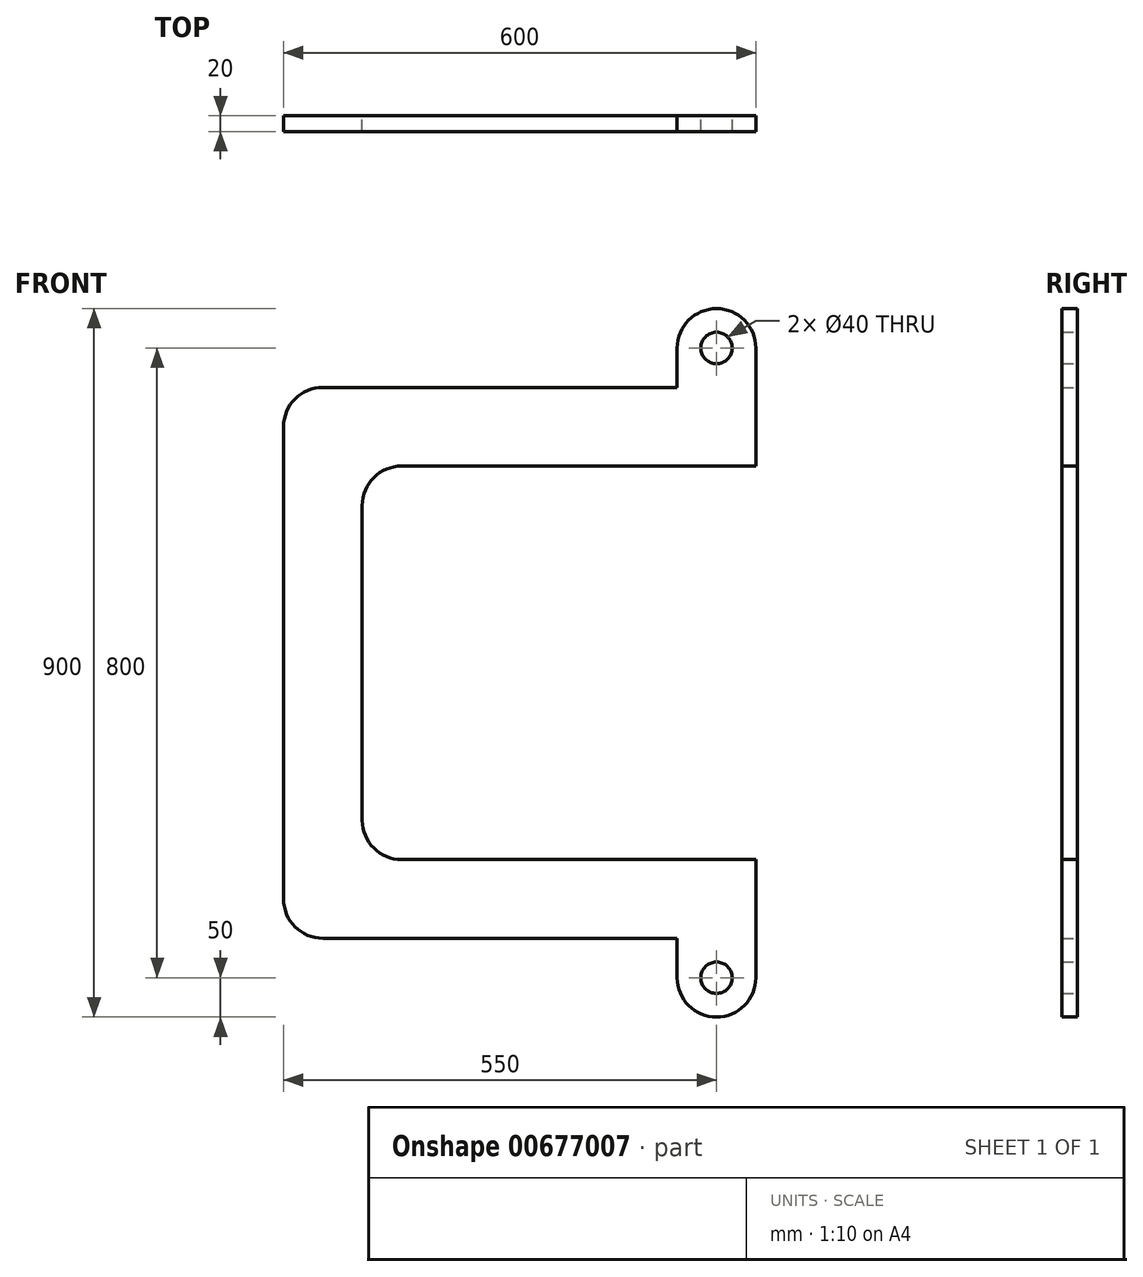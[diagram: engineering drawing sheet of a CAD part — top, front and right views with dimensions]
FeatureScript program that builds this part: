
annotation { "Feature Type Name" : "Feature", "Feature Type Description" : "" }
export const myFeature = defineFeature(function(context is Context, id is Id, definition is map)
    precondition{}
    {
        {
            var Q0;
            Q0=qCreatedBy(makeId("Front.planeOp"),FACE);
            var sketch = newSketch(context, id + "F0", { "sketchPlane" : qUnion([Q0])});
            skLineSegment(sketch, "E0", {"start": v(0, 0) * mm, "end": v(0, 300) * mm});
            skLineSegment(sketch, "E1", {"start": v(50, 350) * mm, "end": v(500, 350) * mm});
            skLineSegment(sketch, "E2", {"start": v(500, 350) * mm, "end": v(500, 400) * mm});
            skLineSegment(sketch, "E3", {"start": v(600, 400) * mm, "end": v(600, 250) * mm});
            skLineSegment(sketch, "E4", {"start": v(600, 250) * mm, "end": v(150, 250) * mm});
            skLineSegment(sketch, "E5", {"start": v(100, 200) * mm, "end": v(100, 0) * mm});
            skArc(sketch, "E6", {"start": v(600, 400) * mm, "mid": v(550, 450) * mm, "end": v(500, 400) * mm});
            skPoint(sketch, "E6.third.point", {"position": v(554.55, 350.2) * mm});
            skCircle(sketch, "E7", {"center": v(550, 400) * mm, "radius": 20 * mm});
            skPoint(sketch, "E8.visualSharp", {"position": v(0, 350) * mm});
            skArc(sketch, "E8.filletArc", {"start": v(50, 350) * mm, "mid": v(14.64, 335.36) * mm, "end": v(0, 300) * mm});
            skPoint(sketch, "E9.visualSharp", {"position": v(100, 250) * mm});
            skArc(sketch, "E9.filletArc", {"start": v(150, 250) * mm, "mid": v(114.64, 235.36) * mm, "end": v(100, 200) * mm});
            skLineSegment(sketch, "E10.MirrorCS", {"start": v(0, 0) * mm, "end": v(0, -300) * mm});
            skLineSegment(sketch, "E11.MirrorCS", {"start": v(100, -200) * mm, "end": v(100, 0) * mm});
            skArc(sketch, "E12.MirrorCS", {"start": v(150, -250) * mm, "mid": v(114.64, -235.36) * mm, "end": v(100, -200) * mm});
            skArc(sketch, "E13.MirrorCS", {"start": v(50, -350) * mm, "mid": v(14.64, -335.36) * mm, "end": v(0, -300) * mm});
            skLineSegment(sketch, "E14.MirrorCS", {"start": v(50, -350) * mm, "end": v(500, -350) * mm});
            skLineSegment(sketch, "E15.MirrorCS", {"start": v(600, -250) * mm, "end": v(150, -250) * mm});
            skLineSegment(sketch, "E16.MirrorCS", {"start": v(500, -350) * mm, "end": v(500, -400) * mm});
            skArc(sketch, "E17.MirrorCS", {"start": v(600, -400) * mm, "mid": v(550, -450) * mm, "end": v(500, -400) * mm});
            skCircle(sketch, "E18.MirrorC", {"center": v(550, -400) * mm, "radius": 20 * mm});
            skLineSegment(sketch, "E19.MirrorCS", {"start": v(600, -400) * mm, "end": v(600, -250) * mm});
            skSolve(sketch);
        }
        {
            var Q0;
            Q0=makeQuery(id+"F0.imprint","IMPRINT",FACE,{"disambiguationData":[TD([[makeQuery(id+"F0.imprint","IMPRINT",EDGE,{"derivedFrom":sQuery(id+"F0.wireOp",EDGE,"E0")}),-1.0]])]});
            extrude(context, id + "F1", {"entities" : qUnion([Q0]), "depth" : 20 * mm, "offsetDistance" : 25 * mm});
        }
    });
